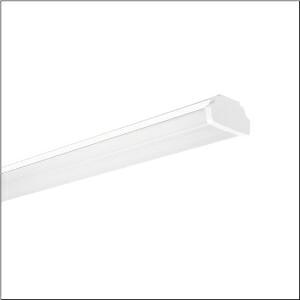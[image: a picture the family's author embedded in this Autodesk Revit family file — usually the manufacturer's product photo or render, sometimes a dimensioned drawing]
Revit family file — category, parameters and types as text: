
# Revit family: modario_r__31_mo_53bm812c1v4075_06f5
name_source: partatom
category: Lighting Fixtures
units: mm (PartAtom-declared; Revit-internal decimal feet)

## family parameters
Cut with Voids When Loaded = No
Host = Face
Light Source = No
Part Type = Normal
Room Calculation Point = No
Round Connector Dimension = Use Diameter
Shared = No

## types (1)
- --- (1 x LED, 7620 lm, 48.9 W, 4000K)
    Apparent Load = 49 VA
    CIE Flux Codes = 47 80 95 92 100
    Color Rendering = 80
    Color Temperature = 4000K
    Default Elevation = 1800 mm
    Description = Modario® 31 MO, luminaire insert, of sheet steel, coil coated, white, length: 1.495mm, width: 81mm, height: 82mm, 5x system unit, system units: 299mm, LED rated luminous flux: 7.620lm, light colour: 840, control gear: ON/OFF Multilumen, CLOi, control gear: ECG Multilumen, with plug, 3-pole, with phase selection, mains connection: 220..240V, AC, 50/60Hz, start of lifetime: 49W, end of service life: 56W, through-wiring accessed according to module size, primary optical cover: cover, of PMMA, light emission: direct distribution, primary light characteristic: symmetric, protection rating (complete): IP20, protection rating (LED compartment): IP50, insulation class (complete): insulation class I (protective earthing), certification: CE, ENEC, VDE, UKCA, impact resistance: IK03, permissible ambient temperature for indoor applications: -35..+30°C, corresponds to IFS (International Featured Standards) requirements for safety and quality in the food industry, reducing of maximum allowable ambient temperature of 5°C with ceiling mounting, packaging unit: 1 piece
    Height = 92 mm
    Lamp = 1 x LED
    Lamp Light Flux = 7620 lm
    Lamp Power = 48.9 W
    Lamp count = 1
    Length = 1495 mm
    Luminous efficacy = 156 lm/W
    Manufacturer = Siteco
    ModVariant = No
    Model = 53BM812C1V4075
    Mounting Place = Ceiling
    Mounting Type = Pendant
    Number of Poles = 1
    OnlyDefault = Yes
    Power Factor = 1
    Product Name = Modario® 31 MO
    Product group = luminaire insert
    ProductGroupID = 901
    Protection Class = Protection class I
    Protection Degree = IP 20
    RLX_Detail_Level = 1
    RLX_Emergency_Light_Flux = 0 lm
    RLX_Emergency_Type = 0
    RLX_Emergency_Type_DB = No
    RlxData = <blob elided: 40113 chars, md5=8a3250b6>
    Socket = socket
    Standby Power = 0 W
    System Light Flux = 7620 lm
    System Power = 49 W
    Type Comments = factory setting: luminous flux: 100 % | (A | C | E) | 107 mA
    Type Image = l_1300283.jpg
    URL = http://relux.com
    VarID = @adj_138191
    Voltage = 0 V
    Weight = 0.00 kg
    Width = 81 mm

## geometry (parser evidence)
native form markers: Blend x4, Sweep x13
no freeform markers — native parametric forms only
